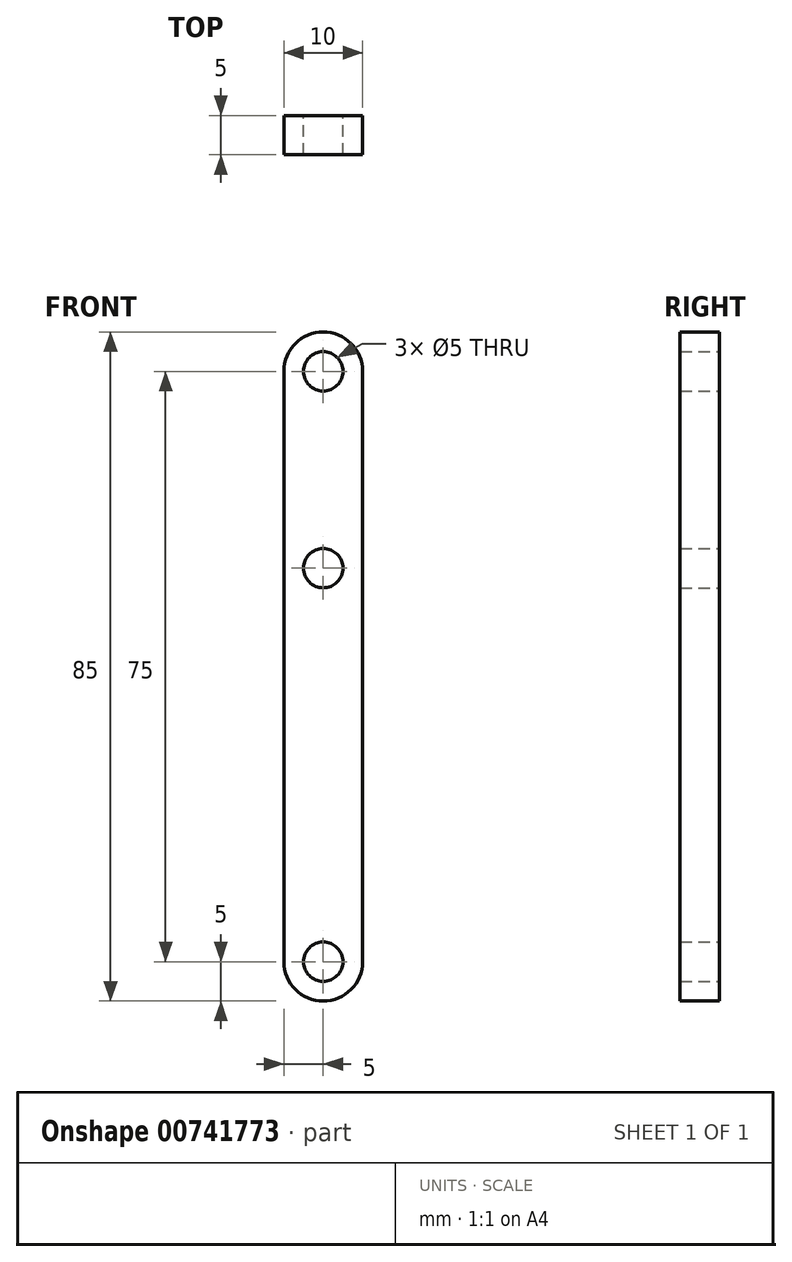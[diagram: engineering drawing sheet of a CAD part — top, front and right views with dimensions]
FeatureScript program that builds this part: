
annotation { "Feature Type Name" : "Feature", "Feature Type Description" : "" }
export const myFeature = defineFeature(function(context is Context, id is Id, definition is map)
    precondition{}
    {
        {
            var Q0;
            Q0=qCreatedBy(makeId("Front.planeOp"),FACE);
            var sketch = newSketch(context, id + "F0", { "sketchPlane" : qUnion([Q0])});
            skLineSegment(sketch, "E0", {"start": v(0, 0) * mm, "end": v(0, 46.13) * mm, "construction": true});
            skArc(sketch, "E1", {"start": v(-5, 0) * mm, "mid": v(0, -5) * mm, "end": v(5, 0) * mm});
            skArc(sketch, "E2", {"start": v(5, 75) * mm, "mid": v(0, 80) * mm, "end": v(-5, 75) * mm});
            skCircle(sketch, "E3", {"center": v(0, 75) * mm, "radius": 2.5 * mm});
            skCircle(sketch, "E4", {"center": v(0, 50) * mm, "radius": 2.5 * mm});
            skCircle(sketch, "E5", {"center": v(0, 0) * mm, "radius": 2.5 * mm});
            skLineSegment(sketch, "E6", {"start": v(-5, 75) * mm, "end": v(-5, 0) * mm});
            skLineSegment(sketch, "E7.MirrorCS", {"start": v(5, 75) * mm, "end": v(5, 0) * mm});
            skSolve(sketch);
        }
        {
            var Q0;
            Q0=makeQuery(id+"F0.imprint","IMPRINT",FACE,{"disambiguationData":[TD([[makeQuery(id+"F0.imprint","IMPRINT",EDGE,{"derivedFrom":sQuery(id+"F0.wireOp",EDGE,"E1")}),1.0]])]});
            extrude(context, id + "F1", {"entities" : qUnion([Q0]), "depth" : 5 * mm, "offsetDistance" : 25 * mm});
        }
    });
